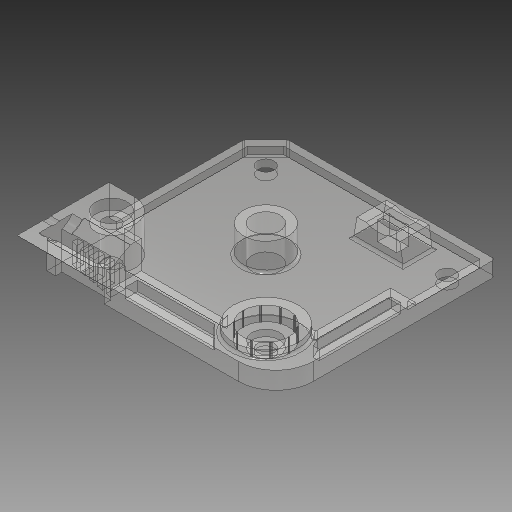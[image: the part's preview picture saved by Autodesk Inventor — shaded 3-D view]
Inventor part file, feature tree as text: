
AUTODESK INVENTOR PART (.ipt)
format: ipt  version: 2018 (Build 220112000, 112)  size: 581,120 bytes
history: native  units: in
note: dims shown in document units (in); Inventor stores cm internally (conversion verified against a paired STEP export)
features: extrude x21, sketch x21, projected_geometry x5, chamfer x3, fillet x3, pattern_circular x1
ambient origin geometry x8: Origin, YZ Plane, XZ Plane, XY Plane, X Axis, Y Axis, Z Axis, Center Point
bodies: Solid1 (feature_tree)
feature tree (54):
  extrude  "Extrusion1"  Depth=1.7323in
  chamfer  "Chamfer2"  Distance=0.1181in
  extrude  "Extrusion2"  Depth=0.1772in TaperAngle=45.0deg
  extrude  "Extrusion3"  Depth=0.1969in
  extrude  "Extrusion4"  Depth=0.815in
  extrude  "Extrusion5"  Depth=0.5118in
  extrude  "Extrusion6"  Depth=0.0787in
  fillet  "Fillet3"  Radius=0.1142in
  pattern_circular  "Circular Pattern1"  Count=10 Angle=360.0deg
  fillet  "Fillet4"  Radius=0.2953in
  extrude  "Extrusion7"  Depth=0.0591in
  extrude  "Extrusion8"  Depth=0.0591in
  extrude  "Extrusion9"  Depth=0.0394in
  extrude  "Extrusion10"  Depth=0.0984in
  extrude  "Extrusion11"  Depth=0.0591in
  chamfer  "Chamfer3"  Distance=0.0591in
  chamfer  "Chamfer4"  Distance=0.0591in
  extrude  "Extrusion12"  Depth=0.0591in
  extrude  "Extrusion13"  Depth=0.0591in
  extrude  "Extrusion14"  Depth=0.0591in TaperAngle=0.0deg
  extrude  "Extrusion15"  Depth=0.1575in
  extrude  "Extrusion16"  Depth=0.2165in TaperAngle=0.0deg
  extrude  "Extrusion17"  Depth=0.1417in
  extrude  "Extrusion18"  Depth=0.1575in
  extrude  "Extrusion19"  Depth=0.1575in
  fillet  "Fillet5"  Radius=0.2165in
  extrude  "Extrusion20"  Depth=0.1575in
  extrude  "Extrusion21"  Depth=0.1575in
  sketch  "Sketch1"  dims[d0=1.811in d1=1.7323in]
  sketch  "Sketch3"  dims[d2=0.2205in]
  projected_geometry  "Projected Loop1"
  sketch  "Sketch4"  dims[d3=1.2205in]
  sketch  "Sketch5"  dims[d4=1.2205in]
  sketch  "Sketch6"  dims[d5=0.1299in d6=0.1181in d7=0.0in]
  sketch  "Sketch7"  dims[d11=0.815in d13=0.1772in d14=0.0787in d15=45.0deg]
  sketch  "Sketch8"  dims[d16=0.1969in d17=1.1024in]
  projected_geometry  "Projected Loop2"
  sketch  "Sketch9"  dims[d18=0.2352in d19=0.815in]
  projected_geometry  "Projected Loop3"
  sketch  "Sketch10"  dims[d20=0.0197in d21=0.0in d22=0.5118in]
  sketch  "Sketch11"  dims[d23=0.0787in d24=0.0in d27=0.3622in d28=0.1142in d29=0.0in]
  sketch  "Sketch12"  dims[d30=0.2165in]
  sketch  "Sketch13"  dims[d31=0.0512in d32=0.0in]
  projected_geometry  "Projected Loop4"
  sketch  "Sketch14"  dims[d33=0.1752in]
  sketch  "Sketch15"  dims[d34=0.0118in]
  sketch  "Sketch16"  dims[d35=0.0512in d36=0.0in]
  sketch  "Sketch17"  dims[d37=0.0057in d38=3.937in d39=360.0deg d41=0.2953in]
  sketch  "Sketch18"  dims[d42=0.0728in d43=0.0591in]
  projected_geometry  "Projected Loop5"
  sketch  "Sketch19"  dims[d44=0.6417in d45=0.0591in]
  sketch  "Sketch20"  dims[d48=0.0787in d49=0.0in d50=0.0394in]
  sketch  "Sketch21"  dims[d51=0.0984in d52=0.6102in]
  sketch  "Sketch22"  dims[d53=0.0394in d54=0.0591in d55=0.0591in d56=0.0591in d57=0.0591in d58=0.0591in d59=0.0591in d60=0.0in d61=0.3543in d62=0.2165in d63=0.0in d64=0.1417in d65=0.2362in d66=0.1299in d67=0.2165in d68=0.0in d69=0.0906in d70=0.1535in d71=0.2303in d72=0.3937in d73=0.124in d74=0.5669in d75=0.1575in d76=0.0in d77=0.1575in d78=0.0787in d79=0.0687in d80=0.1575in d81=0.0787in d82=0.0687in d84=0.2411in d85=45.0deg d87=0.5118in d88=0.0in d89=0.4921in d90=0.5118in d91=0.0in d92=0.5118in d93=0.0in d96=0.3268in d97=0.1831in d98=0.0689in d99=0.0in d100=0.2352in d101=0.315in d102=0.0787in d103=0.0in d104=0.2972in d105=0.0787in d106=0.0in d107=0.248in d108=0.0827in d109=0.0in d110=0.4961in d111=0.3268in d112=0.0827in d113=0.0in d114=0.0197in d115=0.0689in d116=0.0591in d117=0.0669in d118=0.0512in d119=0.0827in d120=0.0in d121=0.1142in d122=0.0453in d124=0.0453in d125=0.0453in d126=0.0453in d127=0.0453in d130=0.0512in d131=0.0374in d132=0.0374in d133=0.0374in d134=0.0374in d136=0.0591in d137=0.0197in d138=0.1575in d139=0.0in]
